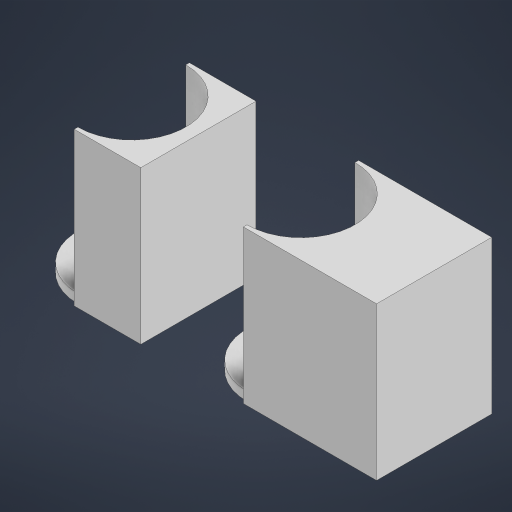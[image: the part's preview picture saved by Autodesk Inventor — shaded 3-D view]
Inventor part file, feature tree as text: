
AUTODESK INVENTOR PART (.ipt)
format: ipt  version: 2023 (Build 270158030, 158C)  size: 185,856 bytes
history: native  units: in
note: dims shown in document units (in); Inventor stores cm internally (conversion verified against a paired STEP export)
features: extrude x2, sketch x1, boolean_combine x1
ambient origin geometry x8: Origin, YZ Plane, XZ Plane, XY Plane, X Axis, Y Axis, Z Axis, Center Point
bodies: Solid2 (feature_tree), Solid3 (feature_tree)
feature tree (4):
  sketch  "Sketch2"  dims[d0=3.8976in d1=1.2598in d2=0.6299in d3=1.9488in d6=1.1811in d7=1.4567in d8=1.1811in d9=1.8504in d10=1.122in d11=0.0in d12=1.6732in d13=0.0in d14=0.0984in d15=0.0in]
  extrude  "Extrusion2"  Depth=1.2598in
  extrude  "Extrusion3"  Depth=0.0984in
  boolean_combine  "Combine1"
